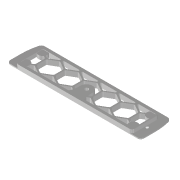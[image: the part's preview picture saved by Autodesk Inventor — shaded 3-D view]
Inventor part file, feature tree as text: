
AUTODESK INVENTOR PART (.ipt)
format: ipt  version: 2021 (Build 250183000, 183)  size: 720,896 bytes
history: native  units: mm
features: projected_geometry x7, extrude x6, sketch x6, chamfer x5, other x2, reference x1
ambient origin geometry x8: Origin, YZ Plane, XZ Plane, XY Plane, X Axis, Y Axis, Z Axis, Center Point
bodies: Volumenkörper1 (feature_tree), Body1 (feature_tree)
feature tree (27):
  extrude  "Extrusion1"  Depth=4.4mm
  extrude  "Extrusion2"  Depth=10.0mm TaperAngle=0.0deg
  extrude  "Extrusion3"  Depth=10.0mm TaperAngle=0.0deg
  chamfer  "Fase1"  Distance=1.0mm Angle=45.0deg
  extrude  "Extrusion4"  Depth=6.4mm
  extrude  "Extrusion5"  Depth=20.549999mm
  chamfer  "Fase2"  Distance=5.925mm
  extrude  "Extrusion6"  Depth=14.325001mm
  chamfer  "Fase3"  Distance=6.4mm
  chamfer  "Fase4"  Distance=6.4mm
  chamfer  "Fase5"  Distance=6.4mm
  sketch  "Skizze1"  dims[d0=14.0mm d1=4.4mm]
  sketch  "Skizze2"  dims[d2=10.0mm d3=0.0mm d4=10.0mm d5=0.0mm]
  projected_geometry  "Projizierte Kontur2"
  sketch  "Skizze3"  dims[d6=4.4mm d7=10.0mm d8=0.0mm d9=1.0mm d10=2.0mm d11=45.0deg]
  reference  "Referenz2"
  sketch  "Skizze4"  dims[d12=3.8mm d13=0.0mm d14=6.4mm]
  sketch  "Skizze5"  dims[d15=125.349999mm d16=20.549999mm]
  projected_geometry  "Projizierte Kontur7"
  projected_geometry  "Projizierte Kontur8"
  sketch  "Skizze7"  dims[d17=125.349999mm d18=5.925mm d19=14.325001mm d20=6.4mm d21=6.4mm d22=6.4mm d23=0.6mm d24=0.0mm d25=1.0mm d26=2.0mm d27=45.0deg d34=0.6mm d35=0.0mm d36=1.5mm d37=2.0mm d38=45.0deg d39=1.0mm d40=2.0mm d41=45.0deg d42=0.6mm d43=2.0mm d44=45.0deg]
  projected_geometry  "Projizierte Kontur9"
  projected_geometry  "Projizierte Kontur10"
  projected_geometry  "Projizierte Kontur11"
  projected_geometry  "Projizierte Kontur12"
  other  "Baugruppe2"
  other  "Exhaust_Housing_Thread_Left:1"
